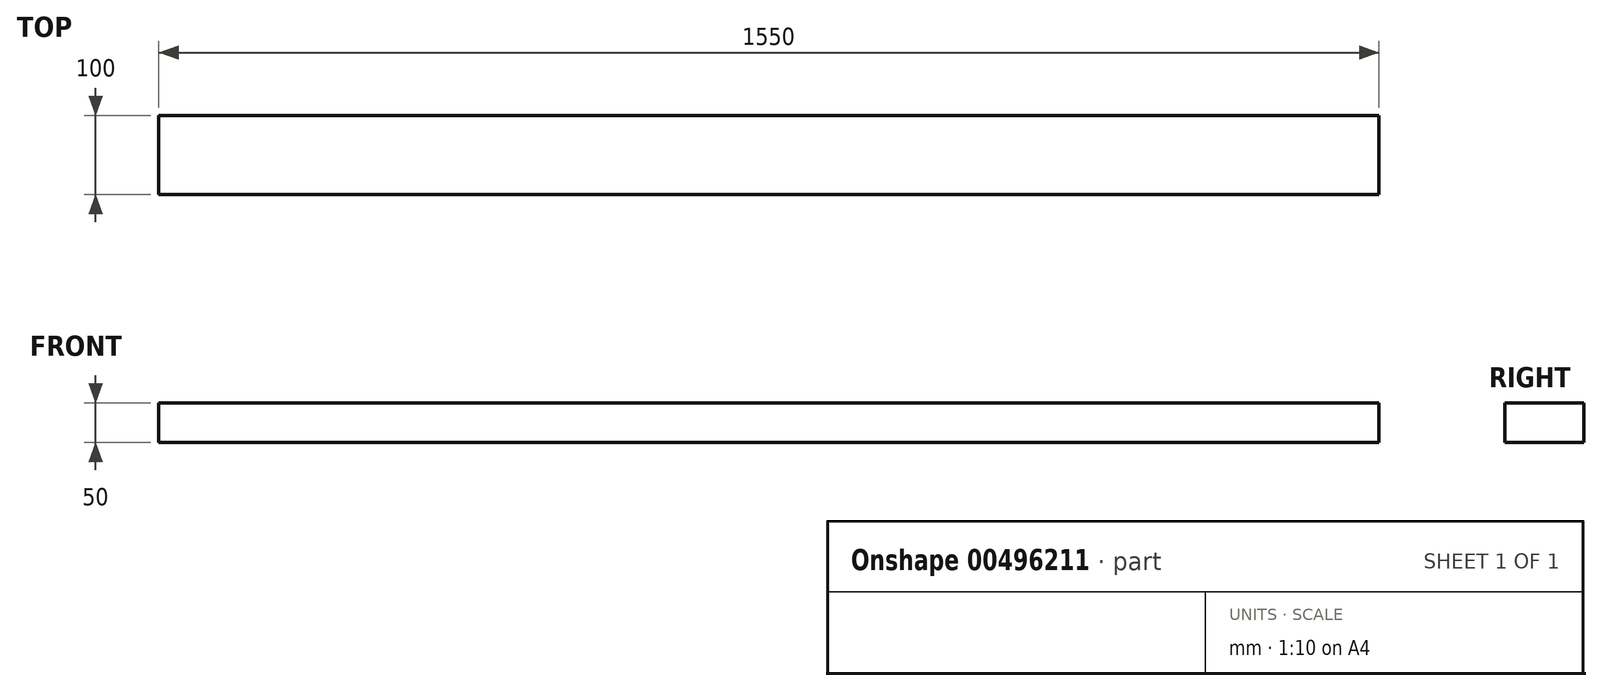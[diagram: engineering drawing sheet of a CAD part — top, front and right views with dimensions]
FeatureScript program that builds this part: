
annotation { "Feature Type Name" : "Feature", "Feature Type Description" : "" }
export const myFeature = defineFeature(function(context is Context, id is Id, definition is map)
    precondition{}
    {
        {
            var Q0;
            Q0=qCreatedBy(makeId("Right.planeOp"),FACE);
            var sketch = newSketch(context, id + "F0", { "sketchPlane" : qUnion([Q0])});
            skLineSegment(sketch, "E0.bottom", {"start": v(0, 0) * mm, "end": v(-100, 0) * mm});
            skLineSegment(sketch, "E0.top", {"start": v(0, 50) * mm, "end": v(-100, 50) * mm});
            skLineSegment(sketch, "E0.left", {"start": v(0, 0) * mm, "end": v(0, 50) * mm});
            skLineSegment(sketch, "E0.right", {"start": v(-100, 0) * mm, "end": v(-100, 50) * mm});
            skSolve(sketch);
        }
        {
            var Q0;
            Q0 = qSketchRegion(id + "F0", true);
            extrude(context, id + "F1", {"entities" : qUnion([Q0]), "endBound" : BoundingType.SYMMETRIC, "depth" : 1550 * mm, "offsetDistance" : 25.4 * mm});
        }
    });
